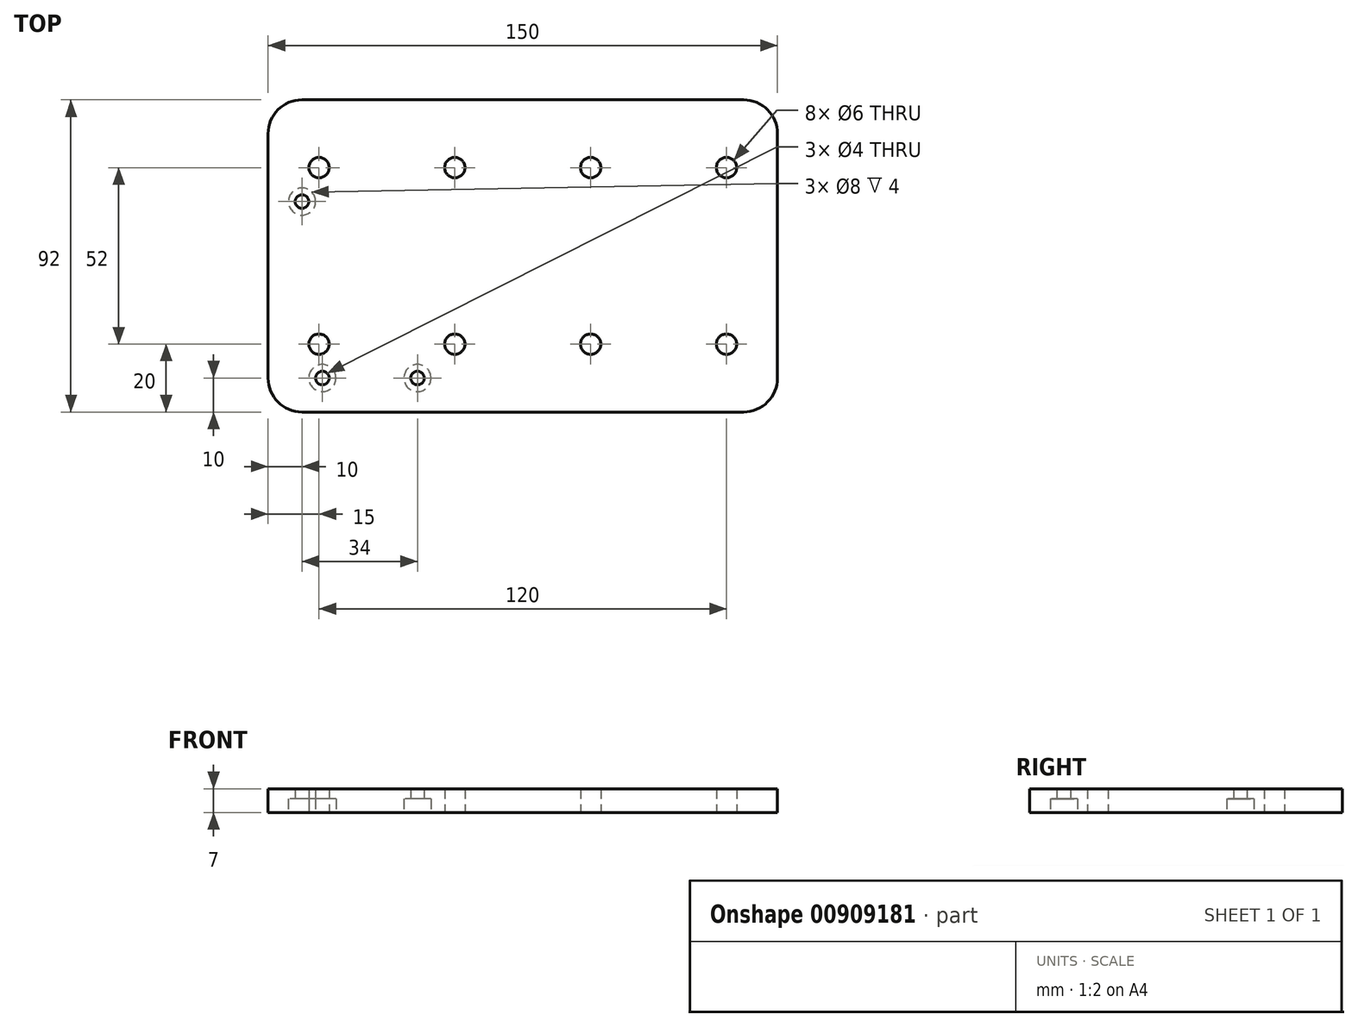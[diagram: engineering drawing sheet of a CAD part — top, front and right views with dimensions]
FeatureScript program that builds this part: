
annotation { "Feature Type Name" : "Feature", "Feature Type Description" : "" }
export const myFeature = defineFeature(function(context is Context, id is Id, definition is map)
    precondition{}
    {
        {
            var Q0;
            Q0=qCreatedBy(makeId("Top.planeOp"),FACE);
            var sketch = newSketch(context, id + "F0", { "sketchPlane" : qUnion([Q0])});
            skLineSegment(sketch, "E0.bottom", {"start": v(0, 0) * mm, "end": v(150, 0) * mm});
            skLineSegment(sketch, "E0.top", {"start": v(0, 92) * mm, "end": v(150, 92) * mm});
            skLineSegment(sketch, "E0.left", {"start": v(0, 0) * mm, "end": v(0, 92) * mm});
            skLineSegment(sketch, "E0.right", {"start": v(150, 0) * mm, "end": v(150, 92) * mm});
            skCircle(sketch, "E1", {"center": v(16, 10) * mm, "radius": 2 * mm});
            skCircle(sketch, "E2", {"center": v(10, 62) * mm, "radius": 2 * mm});
            skCircle(sketch, "E3", {"center": v(44, 10) * mm, "radius": 2 * mm});
            skCircle(sketch, "E4", {"center": v(10, 62) * mm, "radius": 4 * mm});
            skCircle(sketch, "E5", {"center": v(16, 10) * mm, "radius": 4 * mm});
            skCircle(sketch, "E6", {"center": v(44, 10) * mm, "radius": 4 * mm});
            skCircle(sketch, "E7", {"center": v(135, 72) * mm, "radius": 3 * mm});
            skCircle(sketch, "E8", {"center": v(135, 20) * mm, "radius": 3 * mm});
            skCircle(sketch, "E9.1.0.0", {"center": v(95, 72) * mm, "radius": 3 * mm});
            skCircle(sketch, "E9.1.0.1", {"center": v(95, 20) * mm, "radius": 3 * mm});
            skCircle(sketch, "E9.2.0.0", {"center": v(55, 72) * mm, "radius": 3 * mm});
            skCircle(sketch, "E9.2.0.1", {"center": v(55, 20) * mm, "radius": 3 * mm});
            skCircle(sketch, "E9.3.0.0", {"center": v(15, 72) * mm, "radius": 3 * mm});
            skCircle(sketch, "E9.3.0.1", {"center": v(15, 20) * mm, "radius": 3 * mm});
            skLineSegment(sketch, "E9.direction1", {"start": v(140, 10) * mm, "end": v(100, 10) * mm, "construction": true});
            skSolve(sketch);
        }
        {
            var Q0;
            Q0=makeQuery(id+"F0.imprint","IMPRINT",FACE,{"disambiguationData":[TD([[makeQuery(id+"F0.imprint","IMPRINT",EDGE,{"derivedFrom":sQuery(id+"F0.wireOp",EDGE,"E0.bottom")}),1.0]])]});
            var Q1;
            Q1=makeQuery(id+"F0.imprint","IMPRINT",FACE,{"disambiguationData":[TD([[makeQuery(id+"F0.imprint","IMPRINT",EDGE,{"derivedFrom":sQuery(id+"F0.wireOp",EDGE,"E2")}),-1.0]])]});
            var Q2;
            Q2=makeQuery(id+"F0.imprint","IMPRINT",FACE,{"disambiguationData":[TD([[makeQuery(id+"F0.imprint","IMPRINT",EDGE,{"derivedFrom":sQuery(id+"F0.wireOp",EDGE,"E1")}),-1.0]])]});
            var Q3;
            Q3=makeQuery(id+"F0.imprint","IMPRINT",FACE,{"disambiguationData":[TD([[makeQuery(id+"F0.imprint","IMPRINT",EDGE,{"derivedFrom":sQuery(id+"F0.wireOp",EDGE,"E3")}),-1.0]])]});
            extrude(context, id + "F1", {"entities" : qUnion([Q0, Q1, Q2, Q3]), "depth" : 7 * mm, "offsetDistance" : 25 * mm});
        }
        {
            var Q0;
            Q0=makeQuery(id+"F1.opExtrude","SWEPT_EDGE",EDGE,{"disambiguationData":[OSD([sQuery(id+"F0.wireOp",EDGE,"E0.top"),sQuery(id+"F0.wireOp",EDGE,"E0.left")])]});
            var Q1;
            Q1=makeQuery(id+"F1.opExtrude","SWEPT_EDGE",EDGE,{"disambiguationData":[OSD([sQuery(id+"F0.wireOp",EDGE,"E0.bottom"),sQuery(id+"F0.wireOp",EDGE,"E0.left")])]});
            var Q2;
            Q2=makeQuery(id+"F1.opExtrude","SWEPT_EDGE",EDGE,{"disambiguationData":[OSD([sQuery(id+"F0.wireOp",EDGE,"E0.bottom"),sQuery(id+"F0.wireOp",EDGE,"E0.right")])]});
            var Q3;
            Q3=makeQuery(id+"F1.opExtrude","SWEPT_EDGE",EDGE,{"disambiguationData":[OSD([sQuery(id+"F0.wireOp",EDGE,"E0.top"),sQuery(id+"F0.wireOp",EDGE,"E0.right")])]});
            fillet(context, id + "F2", {"entities" : qUnion([Q0, Q1, Q2, Q3]), "tangentPropagation" : true, "radius" : 10 * mm, "defaultsChanged" : true, "vertexSettings" : [], "allowEdgeOverflow" : false});
        }
        {
            var Q0;
            Q0=makeQuery(id+"F0.imprint","IMPRINT",FACE,{"disambiguationData":[TD([[makeQuery(id+"F0.imprint","IMPRINT",EDGE,{"derivedFrom":sQuery(id+"F0.wireOp",EDGE,"E2")}),-1.0]])]});
            var Q1;
            Q1=makeQuery(id+"F0.imprint","IMPRINT",FACE,{"disambiguationData":[TD([[makeQuery(id+"F0.imprint","IMPRINT",EDGE,{"derivedFrom":sQuery(id+"F0.wireOp",EDGE,"E1")}),-1.0]])]});
            var Q2;
            Q2=makeQuery(id+"F0.imprint","IMPRINT",FACE,{"disambiguationData":[TD([[makeQuery(id+"F0.imprint","IMPRINT",EDGE,{"derivedFrom":sQuery(id+"F0.wireOp",EDGE,"E3")}),-1.0]])]});
            extrude(context, id + "F3", {"entities" : qUnion([Q0, Q1, Q2]), "operationType" : NewBodyOperationType.REMOVE, "depth" : 4 * mm, "offsetDistance" : 25 * mm});
        }
    });
